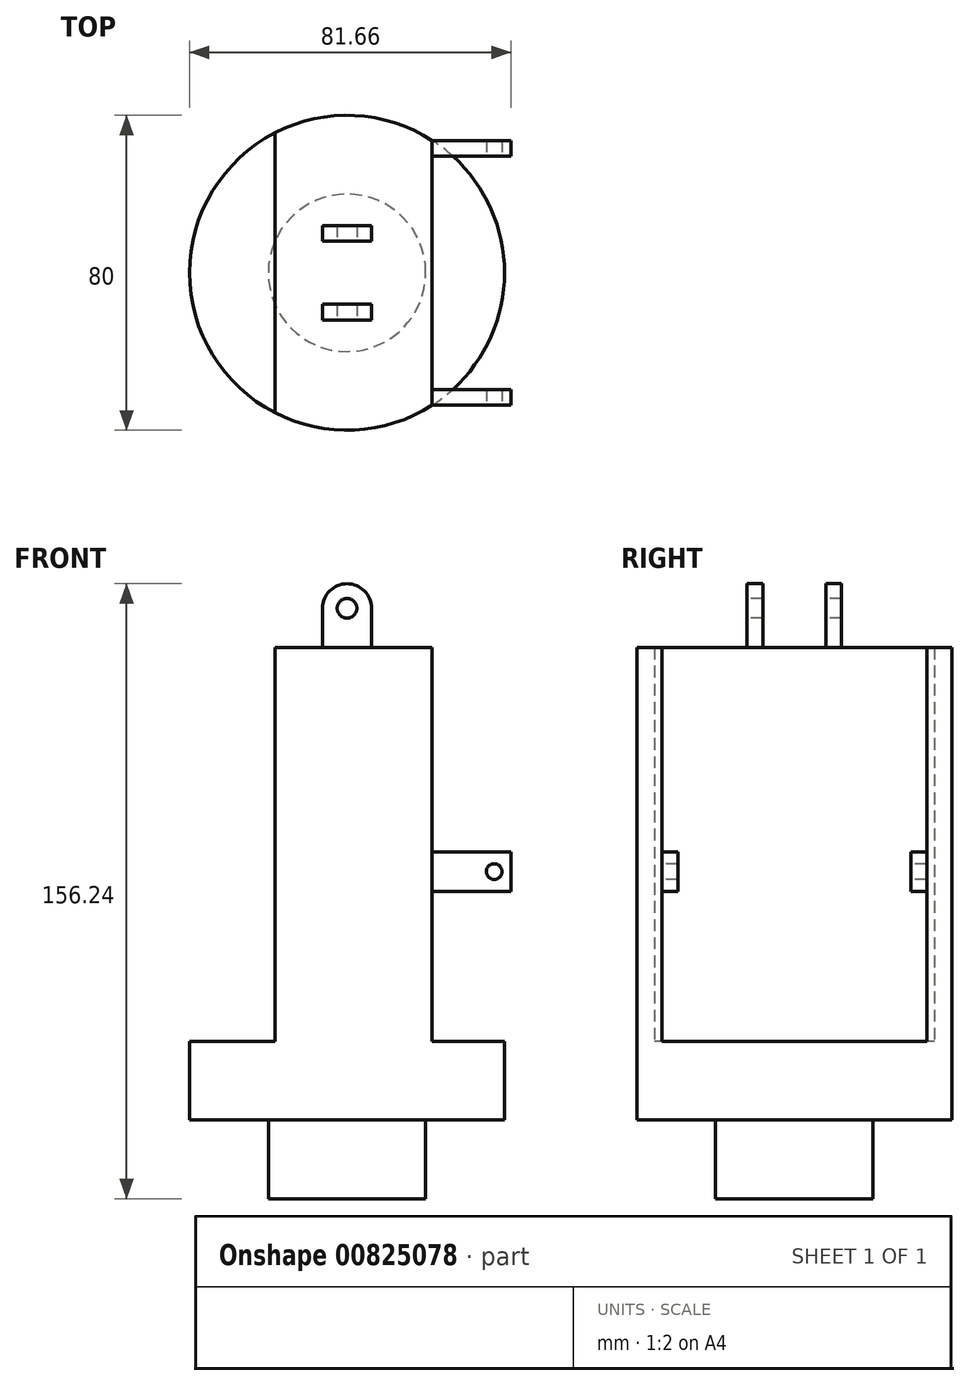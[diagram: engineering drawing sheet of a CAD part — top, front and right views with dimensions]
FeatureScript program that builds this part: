
annotation { "Feature Type Name" : "Feature", "Feature Type Description" : "" }
export const myFeature = defineFeature(function(context is Context, id is Id, definition is map)
    precondition{}
    {
        {
            var Q0;
            Q0=qCreatedBy(makeId("Front.planeOp"),FACE);
            var sketch = newSketch(context, id + "F0", { "sketchPlane" : qUnion([Q0])});
            skLineSegment(sketch, "E0.bottom", {"start": v(0, 0) * mm, "end": v(20, 0) * mm});
            skLineSegment(sketch, "E0.top", {"start": v(0, -20) * mm, "end": v(20, -20) * mm});
            skLineSegment(sketch, "E0.left", {"start": v(0, 0) * mm, "end": v(0, -20) * mm});
            skLineSegment(sketch, "E0.right", {"start": v(20, 0) * mm, "end": v(20, -20) * mm});
            skLineSegment(sketch, "E1.bottom", {"start": v(40, 20) * mm, "end": v(0, 20) * mm});
            skLineSegment(sketch, "E1.top", {"start": v(40, 0) * mm, "end": v(0, 0) * mm});
            skLineSegment(sketch, "E1.left", {"start": v(40, 20) * mm, "end": v(40, 0) * mm});
            skLineSegment(sketch, "E1.right", {"start": v(0, 20) * mm, "end": v(0, 0) * mm});
            skSolve(sketch);
        }
        {
            var Q0;
            Q0=makeQuery(id+"F0.imprint","IMPRINT",FACE,{"disambiguationData":[TD([[makeQuery(id+"F0.imprint","IMPRINT",EDGE,{"derivedFrom":sQuery(id+"F0.wireOp",EDGE,"E0.top")}),1.0]])]});
            var Q1;
            Q1=makeQuery(id+"F0.imprint","IMPRINT",FACE,{"disambiguationData":[TD([[makeQuery(id+"F0.imprint","IMPRINT",EDGE,{"derivedFrom":sQuery(id+"F0.wireOp",EDGE,"E1.bottom")}),1.0]])]});
            var Q2;
            Q2=sQuery(id+"F0.wireOp",EDGE,"E1.right");
            revolve(context, id + "F1", {"surfaceOperationType" : NewSurfaceOperationType.NEW, "entities" : qUnion([Q0, Q1]), "axis" : qUnion([Q2]), "revolveType" : RevolveType.FULL});
        }
        {
            var Q0;
            Q0=makeQuery(id+"F1.opRevolve","SWEPT_FACE",FACE,{"disambiguationData":[OSD([sQuery(id+"F0.wireOp",EDGE,"E1.bottom")])]});
            var sketch = newSketch(context, id + "F2", { "sketchPlane" : qUnion([Q0])});
            skLineSegment(sketch, "E2.bottom", {"start": v(-18.34, 45) * mm, "end": v(21.66, 45) * mm});
            skLineSegment(sketch, "E2.top", {"start": v(-18.34, -45) * mm, "end": v(21.66, -45) * mm});
            skLineSegment(sketch, "E2.left", {"start": v(-18.34, 45) * mm, "end": v(-18.34, -45) * mm});
            skLineSegment(sketch, "E2.right", {"start": v(21.66, 45) * mm, "end": v(21.66, -45) * mm});
            skPoint(sketch, "E2.middle", {"position": v(1.66, 0) * mm});
            skSolve(sketch);
        }
        {
            var Q0;
            {var subQ0=sQuery(id+"F2.wireOp",EDGE,"E2.left");var subQ1=makeQuery(id+"F1.opRevolve","SWEPT_EDGE",EDGE,{"disambiguationData":[OSD([sQuery(id+"F0.wireOp",EDGE,"E1.bottom"),sQuery(id+"F0.wireOp",EDGE,"E1.left")])]});var subQ2=makeQuery(id+"F2.imprint","INTERSECT",VERTEX,{"disambiguationData":[OD(0.0)],"derivedFrom":[subQ1,subQ0]});Q0=makeQuery(id+"F2.imprint","IMPRINT",FACE,{"disambiguationData":[TD([[makeQuery(id+"F2.imprint","IMPRINT",EDGE,{"disambiguationData":[TD([[subQ2,-1.0]])],"derivedFrom":subQ0}),1.0]])]});}
            extrude(context, id + "F3", {"entities" : qUnion([Q0]), "operationType" : NewBodyOperationType.ADD, "depth" : 100 * mm, "offsetDistance" : 25 * mm});
        }
        {
            var Q0;
            Q0=makeQuery(id+"F3.opExtrude","CAP_FACE",FACE,{"disambiguationData":[OSD([sQuery(id+"F0.wireOp",EDGE,"E1.bottom"),sQuery(id+"F0.wireOp",EDGE,"E1.left"),sQuery(id+"F2.wireOp",EDGE,"E2.left"),sQuery(id+"F2.wireOp",EDGE,"E2.right")])],"isStart":false});
            var sketch = newSketch(context, id + "F4", { "sketchPlane" : qUnion([Q0])});
            skLineSegment(sketch, "E3.bottom", {"start": v(-6.24, 8) * mm, "end": v(6.24, 8) * mm});
            skLineSegment(sketch, "E3.top", {"start": v(-6.24, 12) * mm, "end": v(6.24, 12) * mm});
            skLineSegment(sketch, "E3.left", {"start": v(-6.24, 8) * mm, "end": v(-6.24, 12) * mm});
            skLineSegment(sketch, "E3.right", {"start": v(6.24, 8) * mm, "end": v(6.24, 12) * mm});
            skPoint(sketch, "E3.middle", {"position": v(0, 10) * mm});
            skLineSegment(sketch, "E4.MirrorCS", {"start": v(-6.24, -8) * mm, "end": v(-6.24, -12) * mm});
            skLineSegment(sketch, "E5.MirrorCS", {"start": v(-6.24, -12) * mm, "end": v(6.24, -12) * mm});
            skLineSegment(sketch, "E6.MirrorCS", {"start": v(6.24, -8) * mm, "end": v(6.24, -12) * mm});
            skPoint(sketch, "E7.MirrorP", {"position": v(0, -10) * mm});
            skLineSegment(sketch, "E8.MirrorCS", {"start": v(-6.24, -8) * mm, "end": v(6.24, -8) * mm});
            skSolve(sketch);
        }
        {
            var Q0;
            Q0=makeQuery(id+"F4.imprint","IMPRINT",FACE,{"disambiguationData":[TD([[makeQuery(id+"F4.imprint","IMPRINT",EDGE,{"derivedFrom":sQuery(id+"F4.wireOp",EDGE,"E4.MirrorCS")}),1.0]])]});
            var Q1;
            Q1=makeQuery(id+"F4.imprint","IMPRINT",FACE,{"disambiguationData":[TD([[makeQuery(id+"F4.imprint","IMPRINT",EDGE,{"derivedFrom":sQuery(id+"F4.wireOp",EDGE,"E3.bottom")}),1.0]])]});
            extrude(context, id + "F5", {"entities" : qUnion([Q0, Q1]), "operationType" : NewBodyOperationType.ADD, "depth" : 20 * mm, "offsetDistance" : 25 * mm});
        }
        {
            var Q0;
            Q0=makeQuery(id+"F5.opExtrude","SWEPT_FACE",FACE,{"disambiguationData":[OSD([sQuery(id+"F4.wireOp",EDGE,"E5.MirrorCS")])]});
            var sketch = newSketch(context, id + "F6", { "sketchPlane" : qUnion([Q0])});
            skArc(sketch, "E9", {"start": v(6.24, 130) * mm, "mid": v(0, 136.24) * mm, "end": v(-6.24, 130) * mm});
            skCircle(sketch, "E10", {"center": v(0, 130) * mm, "radius": 2.5 * mm});
            skSolve(sketch);
        }
        {
            var Q0;
            {var subQ0=sQuery(id+"F6.wireOp",EDGE,"E9");Q0=makeQuery(id+"F6.imprint","IMPRINT",FACE,{"disambiguationData":[TD([[makeQuery(id+"F6.imprint","IMPRINT",EDGE,{"derivedFrom":subQ0}),-1.0]])]});}
            extrude(context, id + "F7", {"entities" : qUnion([Q0]), "operationType" : NewBodyOperationType.REMOVE, "oppositeDirection" : true, "depth" : 50 * mm, "offsetDistance" : 25 * mm});
        }
        {
            var Q0;
            Q0=makeQuery(id+"F6.imprint","IMPRINT",FACE,{"disambiguationData":[TD([[makeQuery(id+"F6.imprint","IMPRINT",EDGE,{"derivedFrom":sQuery(id+"F6.wireOp",EDGE,"E10")}),1.0]])]});
            extrude(context, id + "F8", {"entities" : qUnion([Q0]), "operationType" : NewBodyOperationType.REMOVE, "oppositeDirection" : true, "depth" : 50 * mm, "offsetDistance" : 25 * mm});
        }
        {
            var Q0;
            Q0=makeQuery(id+"F3.opExtrude","SWEPT_FACE",FACE,{"disambiguationData":[OSD([sQuery(id+"F2.wireOp",EDGE,"E2.right")])]});
            var sketch = newSketch(context, id + "F9", { "sketchPlane" : qUnion([Q0])});
            skLineSegment(sketch, "E11.bottom", {"start": v(-33.63, 68.1) * mm, "end": v(-29.63, 68.1) * mm});
            skLineSegment(sketch, "E11.top", {"start": v(-33.63, 58.1) * mm, "end": v(-29.63, 58.1) * mm});
            skLineSegment(sketch, "E11.left", {"start": v(-33.63, 68.1) * mm, "end": v(-33.63, 58.1) * mm});
            skLineSegment(sketch, "E11.right", {"start": v(-29.63, 68.1) * mm, "end": v(-29.63, 58.1) * mm});
            skLineSegment(sketch, "E12.MirrorCS", {"start": v(29.63, 68.1) * mm, "end": v(29.63, 58.1) * mm});
            skLineSegment(sketch, "E13.MirrorCS", {"start": v(33.63, 68.1) * mm, "end": v(33.63, 58.1) * mm});
            skLineSegment(sketch, "E14.MirrorCS", {"start": v(33.63, 58.1) * mm, "end": v(29.63, 58.1) * mm});
            skLineSegment(sketch, "E15.MirrorCS", {"start": v(33.63, 68.1) * mm, "end": v(29.63, 68.1) * mm});
            skSolve(sketch);
        }
        {
            var Q0;
            Q0=makeQuery(id+"F9.imprint","IMPRINT",FACE,{"disambiguationData":[TD([[makeQuery(id+"F9.imprint","IMPRINT",EDGE,{"derivedFrom":sQuery(id+"F9.wireOp",EDGE,"E11.bottom")}),-1.0]])]});
            extrude(context, id + "F10", {"entities" : qUnion([Q0]), "operationType" : NewBodyOperationType.ADD, "depth" : 20 * mm, "offsetDistance" : 25 * mm});
        }
        {
            var Q0;
            Q0=makeQuery(id+"F9.imprint","IMPRINT",FACE,{"disambiguationData":[TD([[makeQuery(id+"F9.imprint","IMPRINT",EDGE,{"derivedFrom":sQuery(id+"F9.wireOp",EDGE,"E12.MirrorCS")}),1.0]])]});
            extrude(context, id + "F11", {"entities" : qUnion([Q0]), "operationType" : NewBodyOperationType.ADD, "depth" : 20 * mm, "offsetDistance" : 25 * mm});
        }
        {
            var Q0;
            Q0=makeQuery(id+"F10.opExtrude","SWEPT_FACE",FACE,{"disambiguationData":[OSD([sQuery(id+"F9.wireOp",EDGE,"E11.left")])]});
            var sketch = newSketch(context, id + "F12", { "sketchPlane" : qUnion([Q0])});
            skLineSegment(sketch, "E16", {"start": v(41.66, 63.1) * mm, "end": v(37.4, 63.1) * mm});
            skCircle(sketch, "E17", {"center": v(37.4, 63.1) * mm, "radius": 2 * mm});
            skSolve(sketch);
        }
        {
            var Q0;
            Q0=makeQuery(id+"F12.imprint","IMPRINT",FACE,{"disambiguationData":[TD([[makeQuery(id+"F12.imprint","IMPRINT",EDGE,{"derivedFrom":sQuery(id+"F12.wireOp",EDGE,"E17")}),1.0]])]});
            extrude(context, id + "F13", {"entities" : qUnion([Q0]), "operationType" : NewBodyOperationType.REMOVE, "oppositeDirection" : true, "depth" : 100 * mm, "offsetDistance" : 25 * mm});
        }
    });
